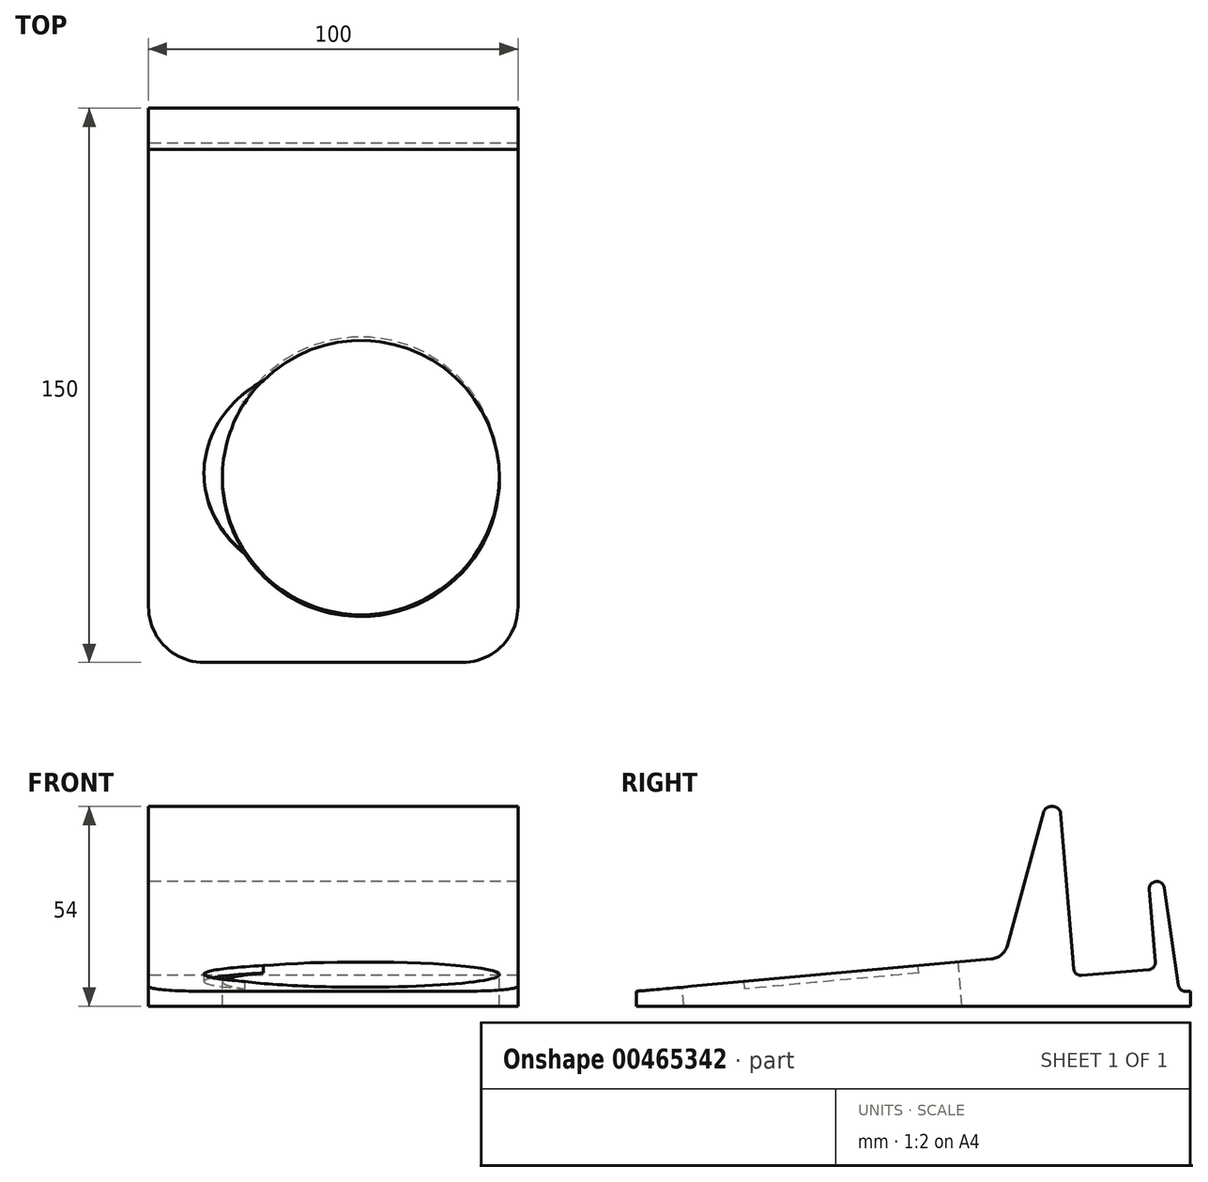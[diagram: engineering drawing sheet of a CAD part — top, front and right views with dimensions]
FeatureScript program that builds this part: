
annotation { "Feature Type Name" : "Feature", "Feature Type Description" : "" }
export const myFeature = defineFeature(function(context is Context, id is Id, definition is map)
    precondition{}
    {
        {
            var Q0;
            Q0=qCreatedBy(makeId("Right.planeOp"),FACE);
            var sketch = newSketch(context, id + "F0", { "sketchPlane" : qUnion([Q0])});
            skLineSegment(sketch, "E0", {"start": v(0, 0) * mm, "end": v(0, 4) * mm});
            skLineSegment(sketch, "E1", {"start": v(150, 4) * mm, "end": v(150, 0) * mm});
            skLineSegment(sketch, "E2", {"start": v(150, 0) * mm, "end": v(0, 0) * mm});
            skLineSegment(sketch, "E3", {"start": v(150, 4) * mm, "end": v(148.73, 4) * mm});
            skLineSegment(sketch, "E4", {"start": v(146.75, 5.71) * mm, "end": v(142.68, 34) * mm});
            skLineSegment(sketch, "E5", {"start": v(142.68, 34) * mm, "end": v(138.72, 33.43) * mm});
            skLineSegment(sketch, "E6", {"start": v(138.72, 33.43) * mm, "end": v(140.53, 12) * mm});
            skPoint(sketch, "E6.endSnap0", {"position": v(140.7, 33.71) * mm});
            skLineSegment(sketch, "E7", {"start": v(138.7, 9.83) * mm, "end": v(120.59, 8.3) * mm});
            skLineSegment(sketch, "E8", {"start": v(118.43, 10.13) * mm, "end": v(114.72, 54) * mm});
            skLineSegment(sketch, "E9", {"start": v(114.72, 54) * mm, "end": v(110.72, 54) * mm});
            skLineSegment(sketch, "E10", {"start": v(110.72, 54) * mm, "end": v(100.47, 16.42) * mm});
            skLineSegment(sketch, "E11", {"start": v(96.1, 12.76) * mm, "end": v(0, 4) * mm});
            skPoint(sketch, "E12.visualSharp", {"position": v(147, 4) * mm});
            skArc(sketch, "E12.filletArc", {"start": v(146.75, 5.71) * mm, "mid": v(147.42, 4.49) * mm, "end": v(148.73, 4) * mm});
            skPoint(sketch, "E13.visualSharp", {"position": v(99.56, 13.07) * mm});
            skArc(sketch, "E13.filletArc", {"start": v(96.1, 12.76) * mm, "mid": v(98.86, 13.9) * mm, "end": v(100.47, 16.42) * mm});
            skPoint(sketch, "E14.visualSharp", {"position": v(118.6, 8.13) * mm});
            skArc(sketch, "E14.filletArc", {"start": v(118.43, 10.13) * mm, "mid": v(119.13, 8.77) * mm, "end": v(120.59, 8.3) * mm});
            skPoint(sketch, "E15.visualSharp", {"position": v(140.7, 10) * mm});
            skArc(sketch, "E15.filletArc", {"start": v(138.7, 9.83) * mm, "mid": v(140.06, 10.53) * mm, "end": v(140.53, 12) * mm});
            skSolve(sketch);
        }
        {
            var Q0;
            Q0=qSketchRegion(id+"F0",true);
            extrude(context, id + "F1", {"entities" : qUnion([Q0]), "depth" : 100 * mm});
        }
        {
            var Q0;
            Q0=makeQuery(id+"F1.opExtrude","CAP_EDGE",EDGE,{"disambiguationData":[OSD([sQuery(id+"F0.wireOp",EDGE,"E0")])],"isStart":false});
            var Q1;
            Q1=makeQuery(id+"F1.opExtrude","CAP_EDGE",EDGE,{"disambiguationData":[OSD([sQuery(id+"F0.wireOp",EDGE,"E0")])],"isStart":true});
            fillet(context, id + "F2", {"entities" : qUnion([Q0, Q1]), "radius" : 15 * mm, "tangentPropagation" : true, "allowEdgeOverflow" : false});
        }
        {
            var Q0;
            Q0=makeQuery(id+"F1.opExtrude","SWEPT_EDGE",EDGE,{"disambiguationData":[OSD([sQuery(id+"F0.wireOp",EDGE,"E9"),sQuery(id+"F0.wireOp",EDGE,"E10")])]});
            var Q1;
            Q1=makeQuery(id+"F1.opExtrude","SWEPT_EDGE",EDGE,{"disambiguationData":[OSD([sQuery(id+"F0.wireOp",EDGE,"E8"),sQuery(id+"F0.wireOp",EDGE,"E9")])]});
            var Q2;
            Q2=makeQuery(id+"F1.opExtrude","SWEPT_EDGE",EDGE,{"disambiguationData":[OSD([sQuery(id+"F0.wireOp",EDGE,"E5"),sQuery(id+"F0.wireOp",EDGE,"E6")])]});
            var Q3;
            Q3=makeQuery(id+"F1.opExtrude","SWEPT_EDGE",EDGE,{"disambiguationData":[OSD([sQuery(id+"F0.wireOp",EDGE,"E4"),sQuery(id+"F0.wireOp",EDGE,"E5")])]});
            fillet(context, id + "F3", {"entities" : qUnion([Q0, Q1, Q2, Q3]), "radius" : 2 * mm, "tangentPropagation" : true, "allowEdgeOverflow" : false});
        }
        {
            var Q0;
            Q0=makeQuery(id+"F1.opExtrude","SWEPT_BODY",BODY,{"disambiguationData":[OSD([sQuery(id+"F0.wireOp",EDGE,"E0"),sQuery(id+"F0.wireOp",EDGE,"E1"),sQuery(id+"F0.wireOp",EDGE,"E2"),sQuery(id+"F0.wireOp",EDGE,"E3"),sQuery(id+"F0.wireOp",EDGE,"E4"),sQuery(id+"F0.wireOp",EDGE,"E5"),sQuery(id+"F0.wireOp",EDGE,"E6"),sQuery(id+"F0.wireOp",EDGE,"E7"),sQuery(id+"F0.wireOp",EDGE,"E8"),sQuery(id+"F0.wireOp",EDGE,"E9"),sQuery(id+"F0.wireOp",EDGE,"E10"),sQuery(id+"F0.wireOp",EDGE,"E11"),sQuery(id+"F0.wireOp",EDGE,"E12.filletArc"),sQuery(id+"F0.wireOp",EDGE,"E13.filletArc"),sQuery(id+"F0.wireOp",EDGE,"E14.filletArc"),sQuery(id+"F0.wireOp",EDGE,"E15.filletArc")])]});
            transform(context, id + "F4", {"entities" : qUnion([Q0]), "transformType" : TransformType.TRANSLATION_3D, "dx" : 0 * mm, "dy" : 0 * mm, "dz" : 0 * mm, "makeCopy" : true});
        }
        {
            var Q0;
            Q0=makeQuery(id+"F4.opPattern","COPY",FACE,{"derivedFrom":makeQuery(id+"F1.opExtrude","SWEPT_FACE",FACE,{"disambiguationData":[OSD([sQuery(id+"F0.wireOp",EDGE,"E11")])]}),"instanceName":"1"});
            var sketch = newSketch(context, id + "F5", { "sketchPlane" : qUnion([Q0])});
            skCircle(sketch, "E16", {"center": v(57.5, 50.36) * mm, "radius": 37.5 * mm});
            skSolve(sketch);
        }
        {
            var Q0;
            Q0=qSketchRegion(id+"F5",true);
            extrude(context, id + "F6", {"entities" : qUnion([Q0]), "operationType" : NewBodyOperationType.REMOVE, "oppositeDirection" : true, "depth" : 25 * mm});
        }
        {
            var Q0;
            Q0=makeQuery(id+"F1.opExtrude","SWEPT_BODY",BODY,{"disambiguationData":[OSD([sQuery(id+"F0.wireOp",EDGE,"E0"),sQuery(id+"F0.wireOp",EDGE,"E1"),sQuery(id+"F0.wireOp",EDGE,"E2"),sQuery(id+"F0.wireOp",EDGE,"E3"),sQuery(id+"F0.wireOp",EDGE,"E4"),sQuery(id+"F0.wireOp",EDGE,"E5"),sQuery(id+"F0.wireOp",EDGE,"E6"),sQuery(id+"F0.wireOp",EDGE,"E7"),sQuery(id+"F0.wireOp",EDGE,"E8"),sQuery(id+"F0.wireOp",EDGE,"E9"),sQuery(id+"F0.wireOp",EDGE,"E10"),sQuery(id+"F0.wireOp",EDGE,"E11"),sQuery(id+"F0.wireOp",EDGE,"E12.filletArc"),sQuery(id+"F0.wireOp",EDGE,"E13.filletArc"),sQuery(id+"F0.wireOp",EDGE,"E14.filletArc"),sQuery(id+"F0.wireOp",EDGE,"E15.filletArc")])]});
            transform(context, id + "F7", {"entities" : qUnion([Q0]), "transformType" : TransformType.TRANSLATION_3D, "dx" : 0 * mm, "dy" : 0 * mm, "dz" : 0 * mm, "makeCopy" : true});
        }
        {
            var Q0;
            Q0=makeQuery(id+"F1.opExtrude","SWEPT_BODY",BODY,{"disambiguationData":[OSD([sQuery(id+"F0.wireOp",EDGE,"E0"),sQuery(id+"F0.wireOp",EDGE,"E1"),sQuery(id+"F0.wireOp",EDGE,"E2"),sQuery(id+"F0.wireOp",EDGE,"E3"),sQuery(id+"F0.wireOp",EDGE,"E4"),sQuery(id+"F0.wireOp",EDGE,"E5"),sQuery(id+"F0.wireOp",EDGE,"E6"),sQuery(id+"F0.wireOp",EDGE,"E7"),sQuery(id+"F0.wireOp",EDGE,"E8"),sQuery(id+"F0.wireOp",EDGE,"E9"),sQuery(id+"F0.wireOp",EDGE,"E10"),sQuery(id+"F0.wireOp",EDGE,"E11"),sQuery(id+"F0.wireOp",EDGE,"E12.filletArc"),sQuery(id+"F0.wireOp",EDGE,"E13.filletArc"),sQuery(id+"F0.wireOp",EDGE,"E14.filletArc"),sQuery(id+"F0.wireOp",EDGE,"E15.filletArc")])]});
            deleteBodies(context, id + "F8", {"entities" : qUnion([Q0])});
        }
        {
            var Q0;
            Q0=makeQuery(id+"F4.opPattern","COPY",BODY,{"derivedFrom":makeQuery(id+"F1.opExtrude","SWEPT_BODY",BODY,{"disambiguationData":[OSD([sQuery(id+"F0.wireOp",EDGE,"E0"),sQuery(id+"F0.wireOp",EDGE,"E1"),sQuery(id+"F0.wireOp",EDGE,"E2"),sQuery(id+"F0.wireOp",EDGE,"E3"),sQuery(id+"F0.wireOp",EDGE,"E4"),sQuery(id+"F0.wireOp",EDGE,"E5"),sQuery(id+"F0.wireOp",EDGE,"E6"),sQuery(id+"F0.wireOp",EDGE,"E7"),sQuery(id+"F0.wireOp",EDGE,"E8"),sQuery(id+"F0.wireOp",EDGE,"E9"),sQuery(id+"F0.wireOp",EDGE,"E10"),sQuery(id+"F0.wireOp",EDGE,"E11"),sQuery(id+"F0.wireOp",EDGE,"E12.filletArc"),sQuery(id+"F0.wireOp",EDGE,"E13.filletArc"),sQuery(id+"F0.wireOp",EDGE,"E14.filletArc"),sQuery(id+"F0.wireOp",EDGE,"E15.filletArc")])]}),"instanceName":"1"});
            deleteBodies(context, id + "F9", {"entities" : qUnion([Q0])});
        }
        {
            var Q0;
            Q0=makeQuery(id+"F7.opPattern","COPY",FACE,{"derivedFrom":makeQuery(id+"F1.opExtrude","SWEPT_FACE",FACE,{"disambiguationData":[OSD([sQuery(id+"F0.wireOp",EDGE,"E11")])]}),"instanceName":"1"});
            var sketch = newSketch(context, id + "F10", { "sketchPlane" : qUnion([Q0])});
            skEllipse(sketch, "E17", {"center": v(50, 51.73) * mm, "majorRadius": 35 * mm, "minorRadius": 30 * mm, "majorAxis": v(1, 0)});
            skFitSpline(sketch, "E18.0", {"points": [v(81.97, 50.41) * mm, v(82.01, 51.73) * mm, v(81.97, 53.05) * mm, v(81.82, 54.79) * mm, v(81.45, 56.94) * mm, v(80.7, 59.46) * mm, v(79.68, 61.92) * mm, v(78.38, 64.29) * mm, v(76.8, 66.55) * mm, v(75.26, 68.34) * mm, v(73.9, 69.7) * mm, v(72.8, 70.67) * mm, v(71.66, 71.6) * mm, v(70.07, 72.78) * mm, v(67.96, 74.12) * mm, v(65.26, 75.5) * mm, v(62.41, 76.66) * mm, v(59.44, 77.57) * mm, v(56.37, 78.24) * mm, v(53.74, 78.57) * mm, v(51.61, 78.7) * mm, v(50, 78.74) * mm, v(48.39, 78.7) * mm, v(46.26, 78.57) * mm, v(43.63, 78.24) * mm, v(40.56, 77.57) * mm, v(37.59, 76.66) * mm, v(34.74, 75.5) * mm, v(32.04, 74.12) * mm, v(29.93, 72.78) * mm, v(28.34, 71.6) * mm, v(27.2, 70.67) * mm, v(26.1, 69.7) * mm, v(24.74, 68.34) * mm, v(23.2, 66.55) * mm, v(21.62, 64.29) * mm, v(20.32, 61.92) * mm, v(19.3, 59.46) * mm, v(18.55, 56.94) * mm, v(18.18, 54.79) * mm, v(18.03, 53.05) * mm, v(17.99, 51.73) * mm, v(18.03, 50.41) * mm, v(18.18, 48.67) * mm, v(18.55, 46.52) * mm, v(19.3, 44) * mm, v(20.32, 41.54) * mm, v(21.62, 39.17) * mm, v(23.2, 36.9) * mm, v(24.74, 35.12) * mm, v(26.1, 33.77) * mm, v(27.2, 32.79) * mm, v(28.34, 31.85) * mm, v(29.93, 30.68) * mm, v(32.04, 29.34) * mm, v(34.74, 27.95) * mm, v(37.59, 26.8) * mm, v(40.56, 25.89) * mm, v(43.63, 25.23) * mm, v(46.26, 24.89) * mm, v(48.39, 24.75) * mm, v(50, 24.72) * mm, v(51.61, 24.75) * mm, v(53.74, 24.89) * mm, v(56.37, 25.23) * mm, v(59.44, 25.89) * mm, v(62.41, 26.8) * mm, v(65.26, 27.95) * mm, v(67.96, 29.34) * mm, v(70.07, 30.68) * mm, v(71.66, 31.85) * mm, v(72.8, 32.79) * mm, v(73.9, 33.77) * mm, v(75.26, 35.12) * mm, v(76.8, 36.9) * mm, v(78.38, 39.17) * mm, v(79.68, 41.54) * mm, v(80.7, 44) * mm, v(81.45, 46.52) * mm, v(81.82, 48.67) * mm, v(81.97, 50.41) * mm, v(82.01, 51.73) * mm, v(81.97, 53.05) * mm, v(81.97, 50.41) * mm]});
            skArc(sketch, "E19", {"start": v(38.97, 49.73) * mm, "mid": v(29.07, 48.73) * mm, "end": v(38.97, 47.73) * mm});
            skArc(sketch, "E20.MirrorC", {"start": v(61.03, 49.73) * mm, "mid": v(70.93, 48.73) * mm, "end": v(61.03, 47.73) * mm});
            skLineSegment(sketch, "E21.0", {"start": v(38.97, 47.73) * mm, "end": v(61.03, 47.73) * mm});
            skLineSegment(sketch, "E22.0", {"start": v(38.97, 49.73) * mm, "end": v(61.03, 49.73) * mm});
            skPoint(sketch, "E23", {"position": v(50, 49.73) * mm});
            skSolve(sketch);
        }
        {
            var Q0;
            Q0 = qSketchRegion(id + "F10", true);
            var Q1;
            Q1=makeQuery(id+"F10.imprint","IMPRINT",FACE,{"disambiguationData":[TD([[makeQuery(id+"F10.imprint","IMPRINT",EDGE,{"derivedFrom":sQuery(id+"F10.wireOp",EDGE,"E19")}),1.0]])]});
            extrude(context, id + "F11", {"entities" : qUnion([Q0, Q1]), "operationType" : NewBodyOperationType.REMOVE, "oppositeDirection" : true, "depth" : 2 * mm});
        }
    });
